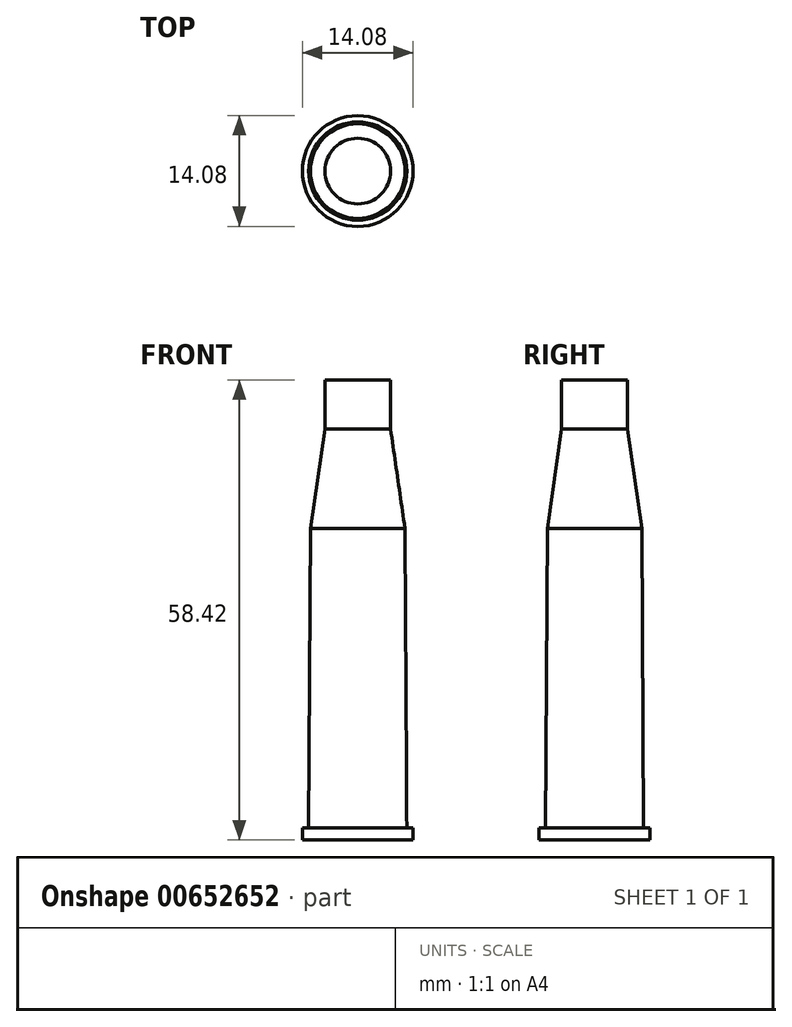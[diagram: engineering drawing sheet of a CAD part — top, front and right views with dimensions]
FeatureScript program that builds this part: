
annotation { "Feature Type Name" : "Feature", "Feature Type Description" : "" }
export const myFeature = defineFeature(function(context is Context, id is Id, definition is map)
    precondition{}
    {
        {
            var Q0;
            Q0=qCreatedBy(makeId("Top.planeOp"),FACE);
            var sketch = newSketch(context, id + "F0", { "sketchPlane" : qUnion([Q0])});
            skCircle(sketch, "E0", {"center": v(0, 0) * mm, "radius": 7.04 * mm});
            skSolve(sketch);
        }
        {
            var Q0;
            Q0=makeQuery(id+"F0.imprint","IMPRINT",FACE,{"disambiguationData":[TD([[makeQuery(id+"F0.imprint","IMPRINT",EDGE,{"derivedFrom":sQuery(id+"F0.wireOp",EDGE,"E0")}),1.0]])]});
            extrude(context, id + "F1", {"entities" : qUnion([Q0]), "depth" : 1.52 * mm, "offsetDistance" : 25.4 * mm});
        }
        {
            var Q0;
            Q0=makeQuery(id+"F1.opExtrude","CAP_FACE",FACE,{"disambiguationData":[OSD([sQuery(id+"F0.wireOp",EDGE,"E0")])],"isStart":false});
            var sketch = newSketch(context, id + "F2", { "sketchPlane" : qUnion([Q0])});
            skCircle(sketch, "E1", {"center": v(0, 0) * mm, "radius": 6.24 * mm});
            skSolve(sketch);
        }
        {
            var Q0;
            Q0=makeQuery(id+"F2.imprint","IMPRINT",FACE,{"disambiguationData":[TD([[makeQuery(id+"F2.imprint","IMPRINT",EDGE,{"derivedFrom":sQuery(id+"F2.wireOp",EDGE,"E1")}),1.0]])]});
            cPlane(context, id + "F3", {"entities" : qUnion([Q0]), "cplaneType" : CPlaneType.OFFSET, "offset" : 38.05 * mm, "width" : 152.4 * mm, "height" : 152.4 * mm});
        }
        {
            var Q0;
            Q0=qCreatedBy(id+"F3.planeOp",FACE);
            var sketch = newSketch(context, id + "F4", { "sketchPlane" : qUnion([Q0])});
            skCircle(sketch, "E2", {"center": v(0, 0) * mm, "radius": 6 * mm});
            skSolve(sketch);
        }
        {
            var Q1;
            Q1=makeQuery(id+"F2.imprint","IMPRINT",FACE,{"disambiguationData":[TD([[makeQuery(id+"F2.imprint","IMPRINT",EDGE,{"derivedFrom":sQuery(id+"F2.wireOp",EDGE,"E1")}),1.0]])]});
            var Q2;
            Q2=makeQuery(id+"F4.imprint","IMPRINT",FACE,{"disambiguationData":[TD([[makeQuery(id+"F4.imprint","IMPRINT",EDGE,{"derivedFrom":sQuery(id+"F4.wireOp",EDGE,"E2")}),1.0]])]});
            loft(context, id + "F5", {"operationType" : NewBodyOperationType.ADD, "sheetProfilesArray" : [{ "sheetProfileEntities" : qUnion([Q1]) }, { "sheetProfileEntities" : qUnion([Q2]) }]});
        }
        {
            var Q0;
            Q0=makeQuery(id+"F5.opLoft","CAP_FACE",FACE,{"disambiguationData":[OSD([makeQuery(id+"F4.imprint","IMPRINT",FACE,{"disambiguationData":[TD([[makeQuery(id+"F4.imprint","IMPRINT",EDGE,{"derivedFrom":sQuery(id+"F4.wireOp",EDGE,"E2")}),1.0]])]})])],"isStart":true});
            cPlane(context, id + "F6", {"entities" : qUnion([Q0]), "cplaneType" : CPlaneType.OFFSET, "offset" : 12.62 * mm, "width" : 152.4 * mm, "height" : 152.4 * mm});
        }
        {
            var Q0;
            Q0=qCreatedBy(id+"F6.planeOp",FACE);
            var sketch = newSketch(context, id + "F7", { "sketchPlane" : qUnion([Q0])});
            skCircle(sketch, "E3", {"center": v(0, 0) * mm, "radius": 4.18 * mm});
            skSolve(sketch);
        }
        {
            var Q1;
            Q1=makeQuery(id+"F5.opLoft","CAP_FACE",FACE,{"disambiguationData":[OSD([makeQuery(id+"F4.imprint","IMPRINT",FACE,{"disambiguationData":[TD([[makeQuery(id+"F4.imprint","IMPRINT",EDGE,{"derivedFrom":sQuery(id+"F4.wireOp",EDGE,"E2")}),1.0]])]})])],"isStart":true});
            var Q2;
            Q2=makeQuery(id+"F7.imprint","IMPRINT",FACE,{"disambiguationData":[TD([[makeQuery(id+"F7.imprint","IMPRINT",EDGE,{"derivedFrom":sQuery(id+"F7.wireOp",EDGE,"E3")}),1.0]])]});
            loft(context, id + "F8", {"operationType" : NewBodyOperationType.ADD, "sheetProfilesArray" : [{ "sheetProfileEntities" : qUnion([Q1]) }, { "sheetProfileEntities" : qUnion([Q2]) }]});
        }
        {
            var Q0;
            Q0=makeQuery(id+"F8.opLoft","CAP_FACE",FACE,{"disambiguationData":[OSD([makeQuery(id+"F7.imprint","IMPRINT",FACE,{"disambiguationData":[TD([[makeQuery(id+"F7.imprint","IMPRINT",EDGE,{"derivedFrom":sQuery(id+"F7.wireOp",EDGE,"E3")}),1.0]])]})])],"isStart":true});
            extrude(context, id + "F9", {"entities" : qUnion([Q0]), "operationType" : NewBodyOperationType.ADD, "depth" : 6.22 * mm, "offsetDistance" : 25.4 * mm});
        }
    });
